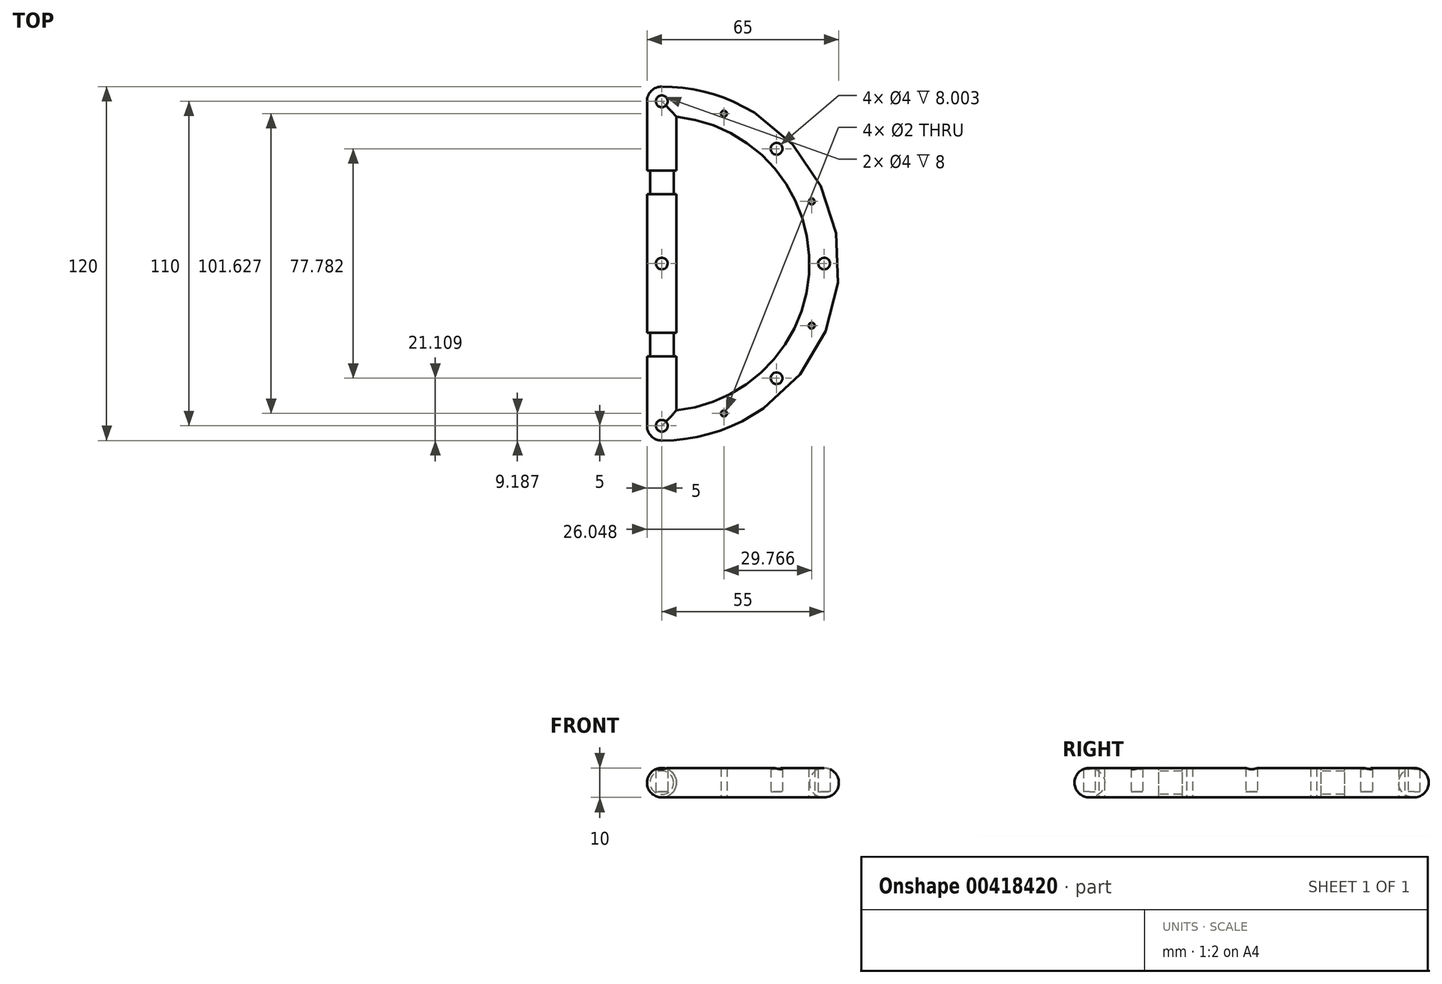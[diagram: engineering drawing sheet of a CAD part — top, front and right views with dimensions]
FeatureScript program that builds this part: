
annotation { "Feature Type Name" : "Feature", "Feature Type Description" : "" }
export const myFeature = defineFeature(function(context is Context, id is Id, definition is map)
    precondition{}
    {
        {
            var Q0;
            Q0=qCreatedBy(makeId("Front.planeOp"),FACE);
            cPlane(context, id + "F0", {"entities" : qUnion([Q0]), "cplaneType" : CPlaneType.OFFSET, "offset" : 110 / 2 * mm, "width" : 150 * mm, "height" : 150 * mm});
        }
        {
            var Q0;
            Q0=qCreatedBy(id+"F0.planeOp",FACE);
            cPlane(context, id + "F1", {"entities" : qUnion([Q0]), "cplaneType" : CPlaneType.OFFSET, "offset" : 110 / 4 * mm, "width" : 150 * mm, "height" : 150 * mm});
        }
        {
            var Q0;
            Q0=qCreatedBy(makeId("Front.planeOp"),FACE);
            cPlane(context, id + "F2", {"entities" : qUnion([Q0]), "cplaneType" : CPlaneType.OFFSET, "offset" : 110 / 4 * mm, "width" : 150 * mm, "height" : 150 * mm});
        }
        {
            var Q0;
            Q0=qCreatedBy(makeId("Front.planeOp"),FACE);
            cPlane(context, id + "F3", {"entities" : qUnion([Q0]), "cplaneType" : CPlaneType.OFFSET, "offset" : 110 * mm, "width" : 150 * mm, "height" : 150 * mm});
        }
        {
            var Q0;
            Q0=qCreatedBy(makeId("Front.planeOp"),FACE);
            var sketch = newSketch(context, id + "F4", { "sketchPlane" : qUnion([Q0])});
            skCircle(sketch, "E0", {"center": v(0, 0) * mm, "radius": 5 * mm});
            skLineSegment(sketch, "E1", {"start": v(0, 5) * mm, "end": v(0, -5) * mm, "construction": true});
            skSolve(sketch);
        }
        {
            var Q0;
            Q0=qCreatedBy(id+"F3.planeOp",FACE);
            var sketch = newSketch(context, id + "F5", { "sketchPlane" : qUnion([Q0])});
            skCircle(sketch, "E2", {"center": v(0, 0) * mm, "radius": 5 * mm});
            skLineSegment(sketch, "E3", {"start": v(0, 5) * mm, "end": v(0, -5) * mm, "construction": true});
            skSolve(sketch);
        }
        {
            var Q0;
            Q0=qSketchRegion(id+"F4",true);
            extrude(context, id + "F6", {"entities" : qUnion([Q0]), "depth" : 110 * mm});
        }
        {
            var Q0;
            Q0=qCreatedBy(makeId("Top.planeOp"),FACE);
            var sketch = newSketch(context, id + "F7", { "sketchPlane" : qUnion([Q0])});
            skArc(sketch, "E4", {"start": v(0, 0) * mm, "mid": v(55, -55) * mm, "end": v(0, -110) * mm});
            skSolve(sketch);
        }
        {
            var Q0;
            Q0=qCreatedBy(makeId("Right.planeOp"),FACE);
            var sketch = newSketch(context, id + "F8", { "sketchPlane" : qUnion([Q0])});
            skCircle(sketch, "E5", {"center": v(-110, 0) * mm, "radius": 5 * mm});
            skSolve(sketch);
        }
        {
            var Q0;
            Q0=qSketchRegion(id+"F8",true);
            var Q1;
            Q1=sQuery(id+"F7.wireOp",EDGE,"E4");
            sweep(context, id + "F9", {"operationType" : NewBodyOperationType.ADD, "profiles" : qUnion([Q0]), "path" : qUnion([Q1])});
        }
        {
            var Q0;
            Q0=makeQuery(id+"F6.opExtrude","CAP_FACE",FACE,{"disambiguationData":[OSD([sQuery(id+"F4.wireOp",EDGE,"E0")])],"isStart":true});
            var Q1;
            Q1=sQuery(id+"F4.wireOp",EDGE,"E0");
            var Q2;
            Q2=makeQuery(id+"F9.boolean.opBoolean","INTERSECT",EDGE,{"derivedFrom":[makeQuery(id+"F6.opExtrude","CAP_FACE",FACE,{"disambiguationData":[OSD([sQuery(id+"F4.wireOp",EDGE,"E0")])],"isStart":true}),makeQuery(id+"F9.opSweep","CAP_FACE",FACE,{"disambiguationData":[OSD([sQuery(id+"F7.wireOp",VERTEX,"E4.start"),sQuery(id+"F8.wireOp",EDGE,"E5")])],"isStart":false})]});
            revolve(context, id + "F10", {"operationType" : NewBodyOperationType.ADD, "entities" : qUnion([Q0]), "surfaceEntities" : qUnion([Q1]), "axis" : qUnion([Q2]), "revolveType" : RevolveType.FULL});
        }
        {
            var Q0;
            Q0=makeQuery(id+"F9.opSweep","CAP_FACE",FACE,{"disambiguationData":[OSD([sQuery(id+"F7.wireOp",VERTEX,"E4.end"),sQuery(id+"F8.wireOp",EDGE,"E5")])],"isStart":true});
            var Q1;
            Q1=sQuery(id+"F5.wireOp",EDGE,"E3");
            revolve(context, id + "F11", {"entities" : qUnion([Q0]), "axis" : qUnion([Q1]), "revolveType" : RevolveType.FULL});
        }
        {
            var Q0;
            Q0=qCreatedBy(makeId("Top.planeOp"),FACE);
            var sketch = newSketch(context, id + "F12", { "sketchPlane" : qUnion([Q0])});
            skCircle(sketch, "E6", {"center": v(0, 0) * mm, "radius": 2 * mm});
            skPoint(sketch, "E7.center", {"position": v(0, -55) * mm});
            skCircle(sketch, "E8.0.4.0", {"center": v(0, -110) * mm, "radius": 2 * mm});
            skCircle(sketch, "E8.0.5.0", {"center": v(38.9, -93.9) * mm, "radius": 2 * mm});
            skCircle(sketch, "E8.0.6.0", {"center": v(55, -55) * mm, "radius": 2 * mm});
            skCircle(sketch, "E8.0.7.0", {"center": v(38.9, -16.1) * mm, "radius": 2 * mm});
            skCircle(sketch, "E9.0.1.0", {"center": v(0, -55) * mm, "radius": 2 * mm});
            skCircle(sketch, "E9.1.1.0", {"center": v(0, -55) * mm, "radius": 2 * mm});
            skLineSegment(sketch, "E9.direction1", {"start": v(0, 0) * mm, "end": v(0, 0) * mm});
            skLineSegment(sketch, "E9.direction2", {"start": v(0, 0) * mm, "end": v(0, -55) * mm, "construction": true});
            skSolve(sketch);
        }
        {
            var Q0;
            Q0=qSketchRegion(id+"F12",true);
            extrude(context, id + "F13", {"entities" : qUnion([Q0]), "operationType" : NewBodyOperationType.REMOVE, "depth" : 25 * mm, "hasSecondDirection" : true, "secondDirectionOppositeDirection" : true, "secondDirectionDepth" : 3 * mm});
        }
        {
            var Q0;
            Q0=qCreatedBy(makeId("Top.planeOp"),FACE);
            var sketch = newSketch(context, id + "F14", { "sketchPlane" : qUnion([Q0])});
            skCircle(sketch, "E10", {"center": v(0, 0) * mm, "radius": 1 * mm, "construction": true});
            skPoint(sketch, "E11.center", {"position": v(0, -55) * mm});
            skCircle(sketch, "E12.0.9.0", {"center": v(21.05, -105.81) * mm, "radius": 1 * mm});
            skCircle(sketch, "E12.0.11.0", {"center": v(50.81, -76.05) * mm, "radius": 1 * mm});
            skCircle(sketch, "E12.0.13.0", {"center": v(50.81, -33.95) * mm, "radius": 1 * mm});
            skCircle(sketch, "E12.0.15.0", {"center": v(21.05, -4.19) * mm, "radius": 1 * mm});
            skSolve(sketch);
        }
        {
            var Q0;
            Q0=qSketchRegion(id+"F14",true);
            extrude(context, id + "F15", {"entities" : qUnion([Q0]), "operationType" : NewBodyOperationType.REMOVE, "endBound" : BoundingType.THROUGH_ALL, "depth" : 25 * mm, "hasSecondDirection" : true, "secondDirectionBound" : SecondDirectionBoundingType.THROUGH_ALL, "secondDirectionOppositeDirection" : true, "secondDirectionDepth" : 25 * mm});
        }
        {
            var Q0;
            Q0=qCreatedBy(id+"F1.planeOp",FACE);
            var sketch = newSketch(context, id + "F16", { "sketchPlane" : qUnion([Q0])});
            skCircle(sketch, "E13", {"center": v(0, 0) * mm, "radius": 5 * mm});
            skCircle(sketch, "E14", {"center": v(0, 0) * mm, "radius": 4 * mm});
            skSolve(sketch);
        }
        {
            var Q0;
            Q0=qCreatedBy(id+"F2.planeOp",FACE);
            var sketch = newSketch(context, id + "F17", { "sketchPlane" : qUnion([Q0])});
            skCircle(sketch, "E15", {"center": v(0, 0) * mm, "radius": 5 * mm});
            skCircle(sketch, "E16", {"center": v(0, 0) * mm, "radius": 4 * mm});
            skSolve(sketch);
        }
        {
            var Q0;
            Q0=qSketchRegion(id+"F16",true);
            var Q1;
            Q1 = qSketchRegion(id + "F17", true);
            extrude(context, id + "F18", {"entities" : qUnion([Q0, Q1]), "operationType" : NewBodyOperationType.REMOVE, "endBound" : BoundingType.SYMMETRIC, "oppositeDirection" : true, "depth" : 8 * mm});
        }
    });
